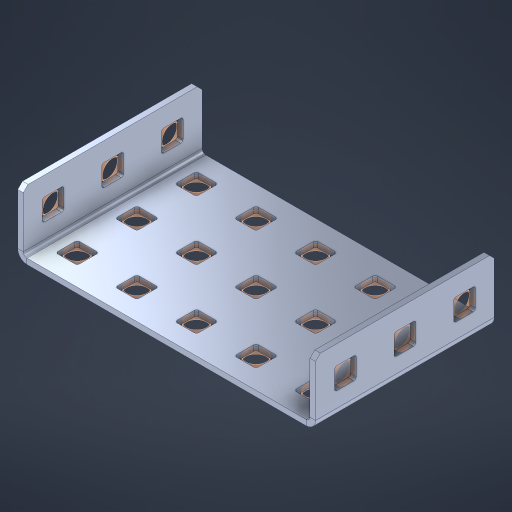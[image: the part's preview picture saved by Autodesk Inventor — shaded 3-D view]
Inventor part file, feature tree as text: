
AUTODESK INVENTOR PART (.ipt)
format: ipt  version: 2023 (Build 270158000, 158)  size: 564,736 bytes
history: native  units: in
note: dims shown in document units (in); Inventor stores cm internally (conversion verified against a paired STEP export)
features: other x26, extrude x20, sheet_metal_op x10, sketch x8, mirror x1, pattern_linear x1, chamfer x1
ambient origin geometry x8: Origin, YZ Plane, XZ Plane, XY Plane, X Axis, Y Axis, Z Axis, Center Point
bodies: Solid1 (feature_tree), Body (feature_tree)
feature tree (67):
  other  "Flange Pattern Plane"
  sheet_metal_op  "Flange Pattern"
  sheet_metal_op  "Body Pattern"
  other  "Arc Length"
  mirror  "Notch Mirror"
  pattern_linear  "Notch Pattern"  Spacing1=0.1875in  [1 undecoded]
  chamfer  "End Chamfer"
  extrude  "Half Cut"  Depth=0.0469in
  sketch  "Sketch1"  dims[d0=2.5in]
  other  "Plate1"
  sketch  "Sketch2"  dims[d1=1.5in]
  other  "Plate2"
  sheet_metal_op  "Bend1"
  sheet_metal_op  "Corner1"
  sketch  "Sketch3"  dims[d2=0.0469in]
  other  "Flange Pattern Sketch"
  sketch  "Sketch7"  dims[d3=0.0469in]
  other  "Srf1"
  other  "Srf2"
  sketch  "Sketch8"  dims[d4=0.0234in]
  sketch  "Sketch9"  dims[d5=0.0938in]
  other  "Srf91"
  sheet_metal_op  "Body Pattern Sketch"
  other  "Srf92"
  sketch  "Sketch13"  dims[d6=0.0469in]
  sketch  "Sketch14"  dims[d7=0.5in d8=90.0deg d9=0.0312in d10=0.1875in d11=0.0469in d12=0.0469in d16=0.182in d17=0.02in d18=0.0469in d19=0.0in d20=0.25in d21=0.25in d46=0.172in d47=1.0in d48=0.0in d49=0.182in d50=0.02in d51=0.25in d52=0.25in d53=0.0469in d54=0.0in d55=0.172in d56=1.0in d57=0.0in d60=1.1811in d62=0.5in d63=1.9685in d65=0.5in d85=0.1227in d86=0.1659in d88=0.04in d89=0.0469in d90=0.0in d91=0.04in d92=0.0491in d95=2.5in d96=0.04in d97=0.25in d98=45.0deg d101=0.0in d102=2.497in d131=2.5in d132=1.1811in d134=0.5in d139=0.5in]
  other  "Srf856"
  other  "Srf1310"
  other  "Srf1311"
  other  "Srf1312"
  other  "Srf1376"
  other  "Srf1377"
  other  "Srf1728"
  other  "Srf1755"
  other  "Srf1942"
  other  "Srf1943"
  other  "Srf1944"
  other  "Srf1945"
  other  "Srf1946"
  other  "Srf1947"
  other  "Srf1948"
  other  "Srf1949"
  other  "Srf1950"
  sheet_metal_op  "Flange Stamp"
  sheet_metal_op  "Flange Circle"
  sheet_metal_op  "Body Stamp"
  sheet_metal_op  "Body Circle"
  sheet_metal_op  "Notch"
  extrude  "ExtrusionSrf2"  Depth=0.0469in
  extrude  "ExtrusionSrf92"  Depth=0.182in
  extrude  "ExtrusionSrf856"  Depth=0.02in
  extrude  "ExtrusionSrf1310"  Depth=0.0469in
  extrude  "ExtrusionSrf1311"  TaperAngle=0.0deg  [1 undecoded]
  extrude  "ExtrusionSrf1312"  Depth=0.25in
  extrude  "ExtrusionSrf1376"  Depth=0.25in
  extrude  "ExtrusionSrf1377"  Depth=0.5in
  extrude  "ExtrusionSrf1728"  Depth=1.0in TaperAngle=0.0deg
  extrude  "ExtrusionSrf1755"  Depth=0.182in
  extrude  "ExtrusionSrf1942"  Depth=0.02in
  extrude  "ExtrusionSrf1943"  Depth=0.25in
  extrude  "ExtrusionSrf1944"  Depth=0.25in
  extrude  "ExtrusionSrf1945"  Depth=0.0469in
  extrude  "ExtrusionSrf1946"  TaperAngle=0.0deg  [1 undecoded]
  extrude  "ExtrusionSrf1947"  Depth=0.5in
  extrude  "ExtrusionSrf1948"  Depth=1.0in TaperAngle=0.0deg
  extrude  "ExtrusionSrf1949"  Depth=1.1811in
  extrude  "ExtrusionSrf1950"  Depth=0.5in
note: 3 required parameter values undecoded (feature->parameter linkage not recoverable at this tier; creation-order binding heuristic only, values carry confidence <= 0.55)
